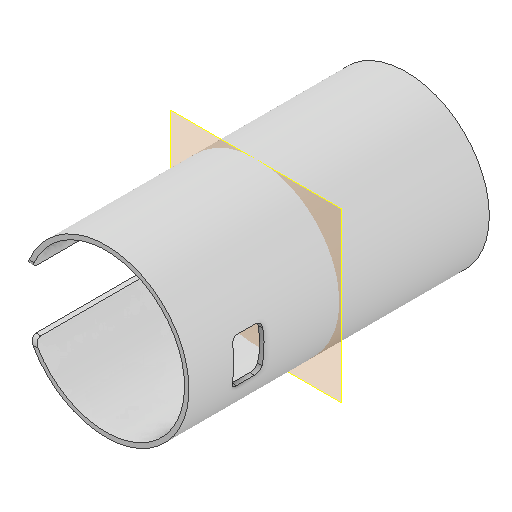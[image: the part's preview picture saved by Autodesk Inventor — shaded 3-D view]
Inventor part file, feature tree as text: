
AUTODESK INVENTOR PART (.ipt)
format: ipt  version: 2022 (Build 260153000, 153)  size: 189,952 bytes
history: native  units: mm
features: other x4, extrude x3, sketch x3, plane x1, fillet x1, projected_geometry x1, reference x1
ambient origin geometry x8: Origin, YZ Plane, XZ Plane, XY Plane, X Axis, Y Axis, Z Axis, Center Point
bodies: Volumenkörper1 (feature_tree)
feature tree (14):
  plane  "Arbeitsebene1"
  extrude  "Extrusion1"  Depth=52.4mm
  extrude  "Extrusion3"  Depth=20.0mm
  fillet  "Rundung1"  Radius=55.0mm
  extrude  "Extrusion4"  Depth=2.0mm
  sketch  "Skizze1"  dims[d0=100.0mm d1=0.0mm d11=52.4mm]
  sketch  "Skizze3"  dims[d12=55.4mm d13=20.0mm d14=55.0mm]
  sketch  "Skizze4"  dims[d15=75.0mm d16=0.0mm d17=2.0mm d18=15.0mm d19=10.0mm d20=15.0mm d21=2.0mm d22=0.0mm d23=0.0mm]
  projected_geometry  "Projizierte Kontur3"
  reference  "Referenz3"
  other  "Planktoscope_Mini_v0.iam"
  other  "Matchboxscope_middle2_v2:1"
  other  "Planktoscope_Mini_Peristalticpump:1"
  other  "Pump_Base_Motor:1"
